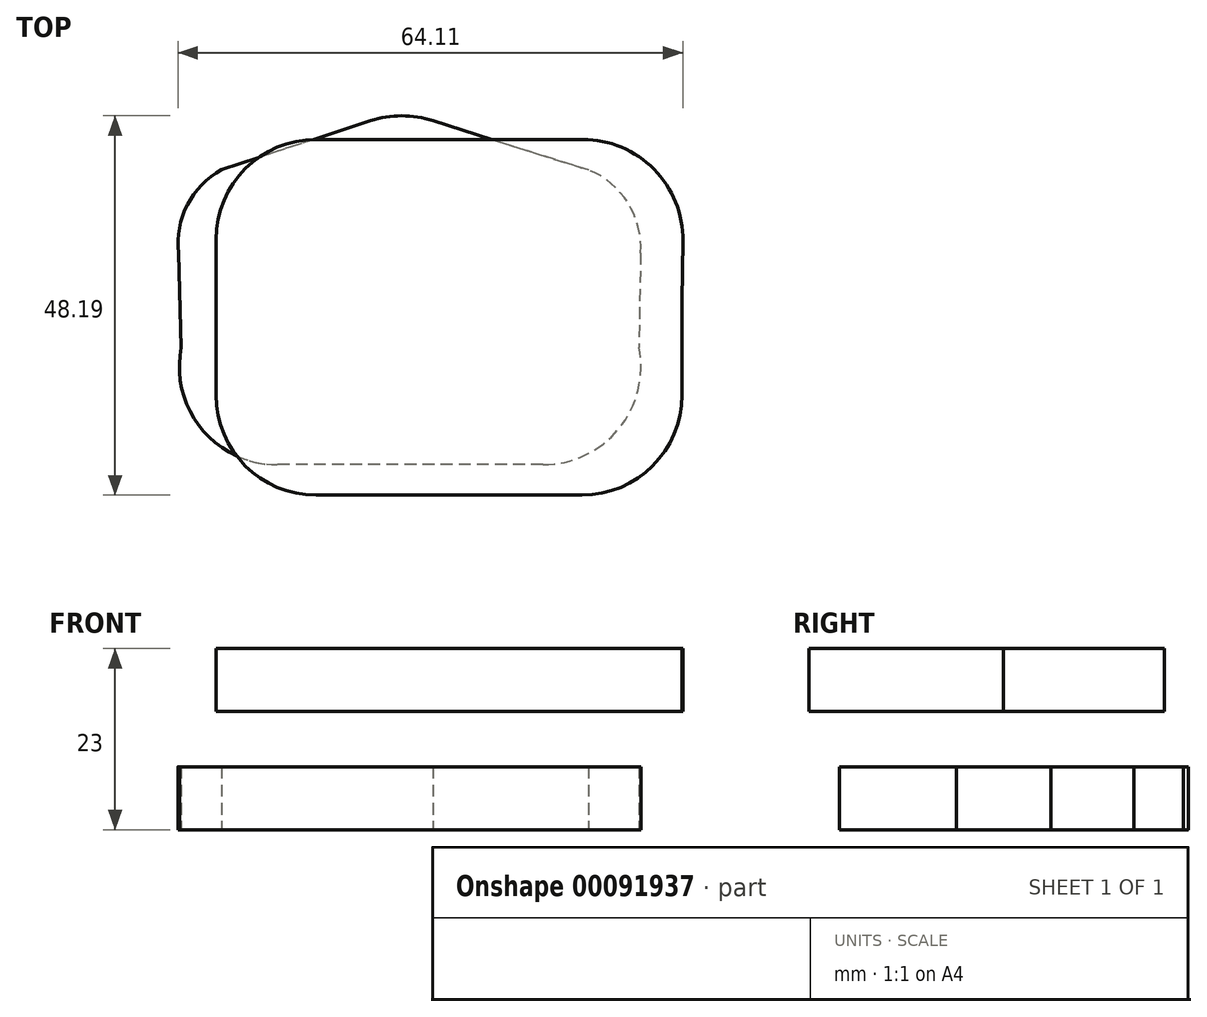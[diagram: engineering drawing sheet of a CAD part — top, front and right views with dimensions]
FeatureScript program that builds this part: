
annotation { "Feature Type Name" : "Feature", "Feature Type Description" : "" }
export const myFeature = defineFeature(function(context is Context, id is Id, definition is map)
    precondition{}
    {
        {
            var Q0;
            Q0=qCreatedBy(makeId("Top.planeOp"),FACE);
            var sketch = newSketch(context, id + "F0", { "sketchPlane" : qUnion([Q0])});
            skLineSegment(sketch, "E0.bottom", {"start": v(16.17, -17.78) * mm, "end": v(-17.6, -17.78) * mm});
            skPoint(sketch, "E0.middle", {"position": v(0, 0) * mm});
            skPoint(sketch, "E1.visualSharp", {"position": v(-30, -17.78) * mm});
            skArc(sketch, "E1.filletArc", {"start": v(-29.78, -2.87) * mm, "mid": v(-27.23, -13.21) * mm, "end": v(-17.6, -17.78) * mm});
            skArc(sketch, "E2.filletArc", {"start": v(16.17, -17.78) * mm, "mid": v(25.8, -13.21) * mm, "end": v(28.34, -2.87) * mm});
            skPoint(sketch, "E3.visualSharp", {"position": v(0, 24.84) * mm});
            skArc(sketch, "E3.filletArc", {"start": v(2.17, 25.91) * mm, "mid": v(-1.79, 26.54) * mm, "end": v(-5.74, 25.91) * mm});
            skArc(sketch, "E4", {"start": v(28.57, 9.13) * mm, "mid": v(26.96, 15.49) * mm, "end": v(21.92, 19.68) * mm});
            skArc(sketch, "E5", {"start": v(-24.68, 19.68) * mm, "mid": v(-29.01, 15.24) * mm, "end": v(-30.12, 9.13) * mm});
            skLineSegment(sketch, "E6", {"start": v(-5.74, 25.91) * mm, "end": v(-24.68, 19.68) * mm});
            skLineSegment(sketch, "E7", {"start": v(2.17, 25.91) * mm, "end": v(21.92, 19.68) * mm});
            skLineSegment(sketch, "E8", {"start": v(28.57, 9.13) * mm, "end": v(28.34, -2.87) * mm});
            skLineSegment(sketch, "E9", {"start": v(-30.12, 9.13) * mm, "end": v(-29.78, -2.87) * mm});
            skPoint(sketch, "E10", {"position": v(28.78, -17.78) * mm});
            skPoint(sketch, "E10.positionSnap0", {"position": v(-0.72, -17.78) * mm});
            skSolve(sketch);
        }
        {
            var Q0;
            Q0=makeQuery(id+"F0.imprint","IMPRINT",FACE,{"disambiguationData":[TD([[makeQuery(id+"F0.imprint","IMPRINT",EDGE,{"derivedFrom":sQuery(id+"F0.wireOp",EDGE,"E0.bottom")}),-1.0]])]});
            extrude(context, id + "F1", {"entities" : qUnion([Q0]), "depth" : 8 * mm});
        }
        {
            var Q0;
            Q0=qCreatedBy(makeId("Top.planeOp"),FACE);
            cPlane(context, id + "F2", {"entities" : qUnion([Q0]), "cplaneType" : CPlaneType.OFFSET, "offset" : 15 * mm, "width" : 152.4 * mm, "height" : 152.4 * mm});
        }
        {
            var Q0;
            Q0=qCreatedBy(id+"F2.planeOp",FACE);
            var sketch = newSketch(context, id + "F3", { "sketchPlane" : qUnion([Q0])});
            skLineSegment(sketch, "E11.bottom", {"start": v(21.1, -21.65) * mm, "end": v(-12.67, -21.65) * mm});
            skPoint(sketch, "E11.middle", {"position": v(-0.06, -3.87) * mm});
            skPoint(sketch, "E12.visualSharp", {"position": v(-30, -21.65) * mm});
            skArc(sketch, "E12.filletArc", {"start": v(-25.37, -8.95) * mm, "mid": v(-21.65, -17.93) * mm, "end": v(-12.67, -21.65) * mm});
            skPoint(sketch, "E13.visualSharp", {"position": v(30, -21.65) * mm});
            skArc(sketch, "E13.filletArc", {"start": v(21.1, -21.65) * mm, "mid": v(30.09, -17.93) * mm, "end": v(33.8, -8.95) * mm});
            skPoint(sketch, "E14.visualSharp", {"position": v(-0.06, 20.97) * mm});
            skLineSegment(sketch, "E15", {"start": v(33.8, 3.05) * mm, "end": v(33.8, -8.95) * mm});
            skLineSegment(sketch, "E16", {"start": v(-25.37, 3.05) * mm, "end": v(-25.37, -8.95) * mm});
            skLineSegment(sketch, "E17", {"start": v(-25.37, 3.05) * mm, "end": v(-25.37, 10.84) * mm});
            skLineSegment(sketch, "E18", {"start": v(-12.67, 23.54) * mm, "end": v(-3.96, 23.54) * mm});
            skLineSegment(sketch, "E19", {"start": v(3.96, 23.54) * mm, "end": v(21.22, 23.54) * mm});
            skLineSegment(sketch, "E20", {"start": v(33.92, 10.65) * mm, "end": v(33.8, 3.05) * mm});
            skLineSegment(sketch, "E21", {"start": v(-3.96, 23.54) * mm, "end": v(3.96, 23.54) * mm});
            skPoint(sketch, "E22.visualSharp", {"position": v(-25.37, 23.54) * mm});
            skArc(sketch, "E22.filletArc", {"start": v(-12.67, 23.54) * mm, "mid": v(-21.65, 19.82) * mm, "end": v(-25.37, 10.84) * mm});
            skPoint(sketch, "E23.visualSharp", {"position": v(34.11, 23.54) * mm});
            skArc(sketch, "E23.filletArc", {"start": v(33.92, 10.65) * mm, "mid": v(30.27, 19.75) * mm, "end": v(21.22, 23.54) * mm});
            skSolve(sketch);
        }
        {
            var Q0;
            Q0=makeQuery(id+"F3.imprint","IMPRINT",FACE,{"disambiguationData":[TD([[makeQuery(id+"F3.imprint","IMPRINT",EDGE,{"derivedFrom":sQuery(id+"F3.wireOp",EDGE,"E11.bottom")}),-1.0]])]});
            extrude(context, id + "F4", {"entities" : qUnion([Q0]), "depth" : 8 * mm});
        }
    });
